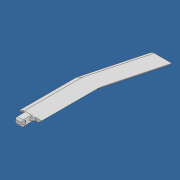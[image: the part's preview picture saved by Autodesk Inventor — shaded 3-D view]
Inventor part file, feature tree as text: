
AUTODESK INVENTOR PART (.ipt)
format: ipt  version: 2022 (Build 260153000, 153)  size: 194,560 bytes
history: native  units: in
note: dims shown in document units (in); Inventor stores cm internally (conversion verified against a paired STEP export)
features: sketch x8, extrude x4, chamfer x3, fillet x2, plane x2, loft x2
ambient origin geometry x8: Origin, YZ Plane, XZ Plane, XY Plane, X Axis, Y Axis, Z Axis, Center Point
bodies: Solid1 (feature_tree)
feature tree (21):
  extrude  "Extrusion1"  Depth=0.7874in
  extrude  "Extrusion2"  Depth=0.1969in
  fillet  "Fillet1"  [1 undecoded]
  fillet  "Fillet2"  Radius=0.0197in
  plane  "Work Plane1"
  plane  "Work Plane2"
  loft  "Loft4"
  sketch  "Sketch9"  dims[d31=0.1969in d32=0.5906in]
  extrude  "Extrusion3"  TaperAngle=0.0deg  [1 undecoded]
  extrude  "Extrusion4"  Depth=0.1969in
  chamfer  "Chamfer1"  Distance=0.3937in
  loft  "Loft5"
  chamfer  "Chamfer2"  Angle=90.0deg  [1 undecoded]
  chamfer  "Chamfer3"  Angle=90.0deg  [1 undecoded]
  sketch  "Sketch1"  dims[d0=0.3937in d1=0.7874in]
  sketch  "Sketch2"  dims[d2=0.3937in d3=0.0in d4=0.1969in d5=0.0in d6=0.0in d7=0.0197in]
  sketch  "Sketch7"  dims[d8=0.1181in d12=-0.0984in]
  sketch  "Sketch8"  dims[d13=-0.0984in d30=0.0in]
  sketch  "Sketch10"  dims[d33=3.937in]
  sketch  "Sketch11"  dims[d34=0.0in]
  sketch  "Sketch12"  dims[d35=0.5906in d36=0.3937in d37=3.937in d38=0.0in d39=90.0deg d40=0.0in d41=90.0deg d42=0.1969in d43=0.1969in d44=0.1969in d45=0.0in d46=0.1969in d47=0.0in d48=0.1969in d49=0.0492in d50=45.0deg d52=15.0deg d53=3.937in d54=3.937in d55=15.0deg d56=0.0in d57=90.0deg d58=0.0in d59=90.0deg d60=0.0984in d61=0.0492in d62=45.0deg d63=0.0984in d64=0.0492in d65=45.0deg]
note: 4 required parameter values undecoded (feature->parameter linkage not recoverable at this tier; creation-order binding heuristic only, values carry confidence <= 0.55)
